# Revit family: Lavatory-TOTO-Supreme-LPT241(G)
name_source: partatom
category: Plumbing Fixtures
revit_build: Autodesk Revit Architecture 2013 (Build: 20130531_2115(x64)
units: mm (PartAtom-declared; Revit-internal decimal feet)

## types (2) — shared parameters
04 CSI = 22 42 16
95 CSI = 15410
ADA Compliant = No
Assembly Code = D2010310
Basin Depth = 1' - 1 1/4"
Basin Diameter = 0' - 0"
Basin Width = 1' - 8 1/2"
CAD Drawing URL = http://assets.totousa.com
Certifications = IAPMO(cUPC), State of Massachusetts , City of Los Angeles, and others
Code Compliance = UPC, IPC, NSPC, NPC Canada, and others
Cold Water Connection Radius = 0' - 0 1/4"
Cold Water Connector = Cold Water Connection
Color Availability = #01 Cotton,#03 Bone,#11 Colonial White,#12 Sedona Beige,#51 Ebony(not available in SanaGloss)
Default Elevation = 0' - 0"
Depth = 1' - 7 5/8"
Finish = Vitreous China - TOTO - 01 Cotton
Height = 2' - 11 1/8"
Hot Water Connection Radius = 0' - 0 1/4"
Hot Water Connector = Hot Water Connection
Industry Standards = Meets and exceeds ASME A112.19.2/CSA B45.1
Manufacturer = TOTO USA, Inc.
Manufacturer Fax = (770) 282-0002
Material = Vitreous china
Sanitary Connector = Sanitary Connection
Series = Supreme
Shipping Weight = 34.00 lb
Spec Sheet URL = http://assets.totousa.com
Subcategory = Lavatories
Toto BIM Number = BM-00370
URL = http://www.totousa.com
Warranty = One Year Limited Warranty
Warranty URL = http://www.totousa.com
Waste Connection NPT Radius = 0' - 0 5/8"
Width = 1' - 10 7/8"

## per-type parameters (varying)
| type | Description | SanaGloss |
| LPT241 | Supreme® Pedestal Lavatory | No |
| LPT241G | Supreme® Pedestal Lavatory - with SanaGloss | Yes |

note: column(s) folded — value = type name in every type: Model

## geometry (parser evidence)
native form markers: Blend x4, Sweep x3
no freeform markers — native parametric forms only
